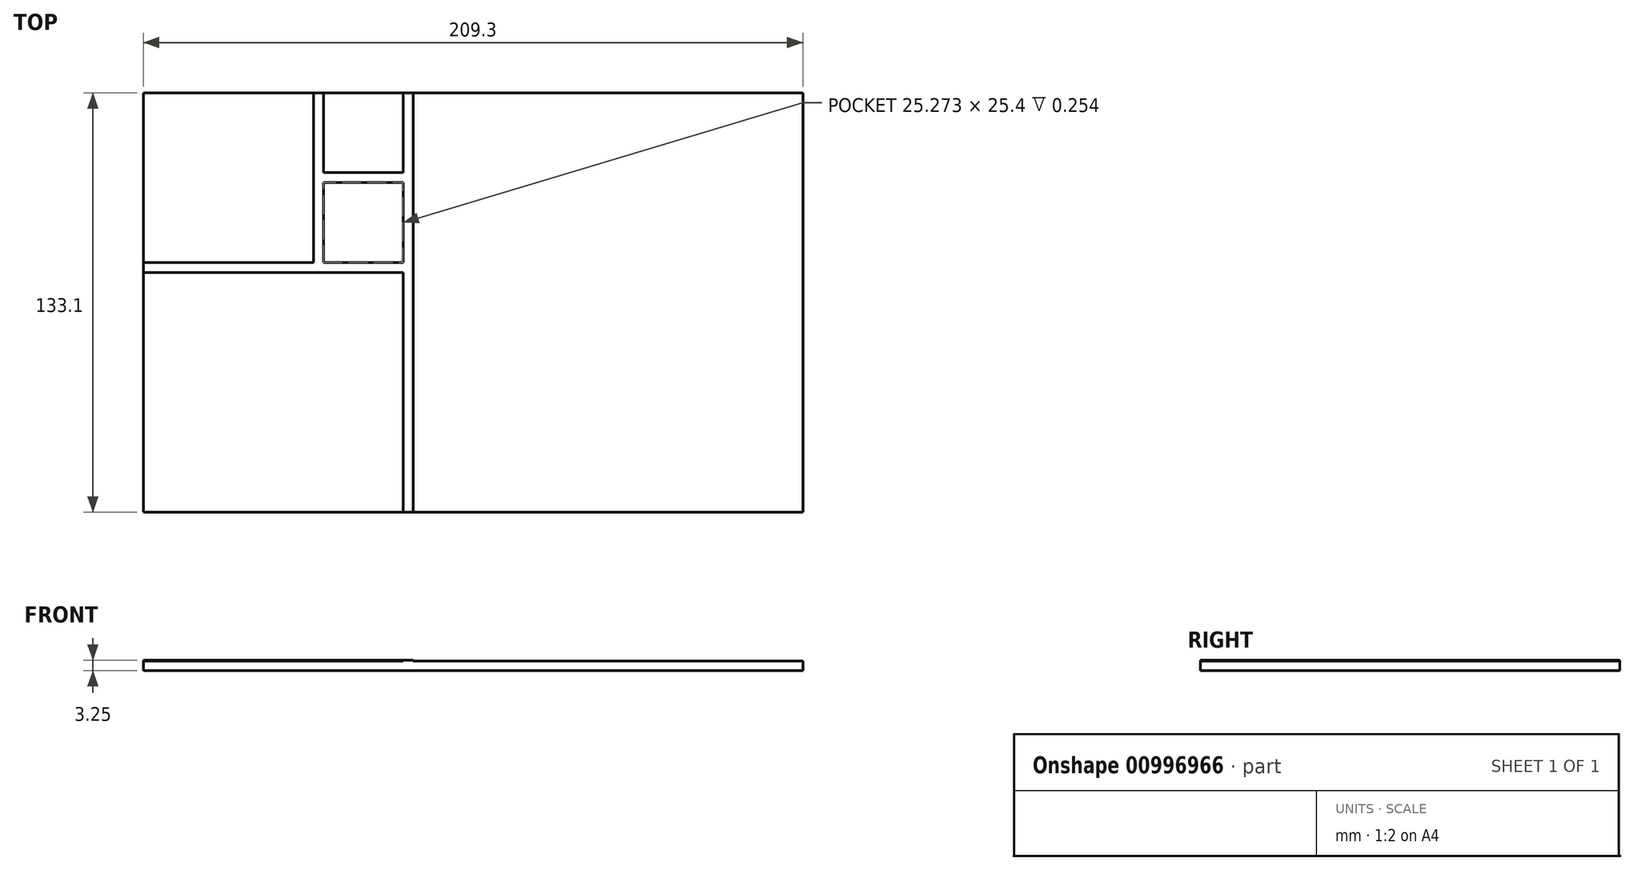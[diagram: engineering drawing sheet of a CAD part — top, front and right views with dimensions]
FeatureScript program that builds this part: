
annotation { "Feature Type Name" : "Feature", "Feature Type Description" : "" }
export const myFeature = defineFeature(function(context is Context, id is Id, definition is map)
    precondition{}
    {
        {
            var Q0;
            Q0=qCreatedBy(makeId("Top.planeOp"),FACE);
            var sketch = newSketch(context, id + "F0", { "sketchPlane" : qUnion([Q0])});
            skLineSegment(sketch, "E0.bottom", {"start": v(104.65, -66.55) * mm, "end": v(-104.65, -66.55) * mm});
            skLineSegment(sketch, "E0.top", {"start": v(104.65, 66.55) * mm, "end": v(-104.65, 66.55) * mm});
            skLineSegment(sketch, "E0.left", {"start": v(104.65, -66.55) * mm, "end": v(104.65, 66.55) * mm});
            skLineSegment(sketch, "E0.right", {"start": v(-104.65, -66.55) * mm, "end": v(-104.65, 66.55) * mm});
            skPoint(sketch, "E0.middle", {"position": v(0, 0) * mm});
            skSolve(sketch);
        }
        {
            var Q0;
            Q0=qSketchRegion(id+"F0",true);
            extrude(context, id + "F1", {"entities" : qUnion([Q0]), "depth" : 3 * mm, "offsetDistance" : 25.4 * mm});
        }
        {
            var Q0;
            Q0=makeQuery(id+"F1.opExtrude","CAP_FACE",FACE,{"disambiguationData":[OSD([sQuery(id+"F0.wireOp",EDGE,"E0.bottom"),sQuery(id+"F0.wireOp",EDGE,"E0.top"),sQuery(id+"F0.wireOp",EDGE,"E0.left"),sQuery(id+"F0.wireOp",EDGE,"E0.right")])],"isStart":false});
            var sketch = newSketch(context, id + "F2", { "sketchPlane" : qUnion([Q0])});
            skLineSegment(sketch, "E1", {"start": v(-50.67, 66.55) * mm, "end": v(-50.67, 12.7) * mm});
            skLineSegment(sketch, "E2", {"start": v(-50.67, 12.7) * mm, "end": v(-104.65, 12.7) * mm});
            skLineSegment(sketch, "E3", {"start": v(-104.65, 12.7) * mm, "end": v(-104.65, 9.52) * mm});
            skLineSegment(sketch, "E4", {"start": v(-104.65, 9.52) * mm, "end": v(-22.22, 9.53) * mm});
            skLineSegment(sketch, "E5", {"start": v(-22.22, 9.53) * mm, "end": v(-22.22, -66.55) * mm});
            skLineSegment(sketch, "E6", {"start": v(-22.22, -66.55) * mm, "end": v(-19.05, -66.55) * mm});
            skLineSegment(sketch, "E7", {"start": v(-19.05, -66.55) * mm, "end": v(-19.05, 66.55) * mm});
            skLineSegment(sketch, "E8", {"start": v(-50.67, 66.55) * mm, "end": v(-47.5, 66.55) * mm});
            skLineSegment(sketch, "E9", {"start": v(-47.5, 66.55) * mm, "end": v(-47.5, 41.28) * mm});
            skLineSegment(sketch, "E10", {"start": v(-47.5, 41.28) * mm, "end": v(-22.22, 41.28) * mm});
            skLineSegment(sketch, "E11", {"start": v(-22.22, 41.28) * mm, "end": v(-22.23, 66.55) * mm});
            skLineSegment(sketch, "E12", {"start": v(-22.22, 66.55) * mm, "end": v(-19.05, 66.55) * mm});
            skLineSegment(sketch, "E13", {"start": v(-47.5, 38.1) * mm, "end": v(-47.5, 12.7) * mm});
            skLineSegment(sketch, "E14", {"start": v(-47.5, 12.7) * mm, "end": v(-22.22, 12.7) * mm});
            skLineSegment(sketch, "E15", {"start": v(-22.22, 12.7) * mm, "end": v(-22.23, 38.1) * mm});
            skLineSegment(sketch, "E16", {"start": v(-22.23, 38.1) * mm, "end": v(-47.5, 38.1) * mm});
            skSolve(sketch);
        }
        {
            var Q0;
            Q0=qSketchRegion(id+"F2",true);
            extrude(context, id + "F3", {"entities" : qUnion([Q0]), "operationType" : NewBodyOperationType.ADD, "depth" : 0.25 * mm, "offsetDistance" : 25.4 * mm});
        }
    });
